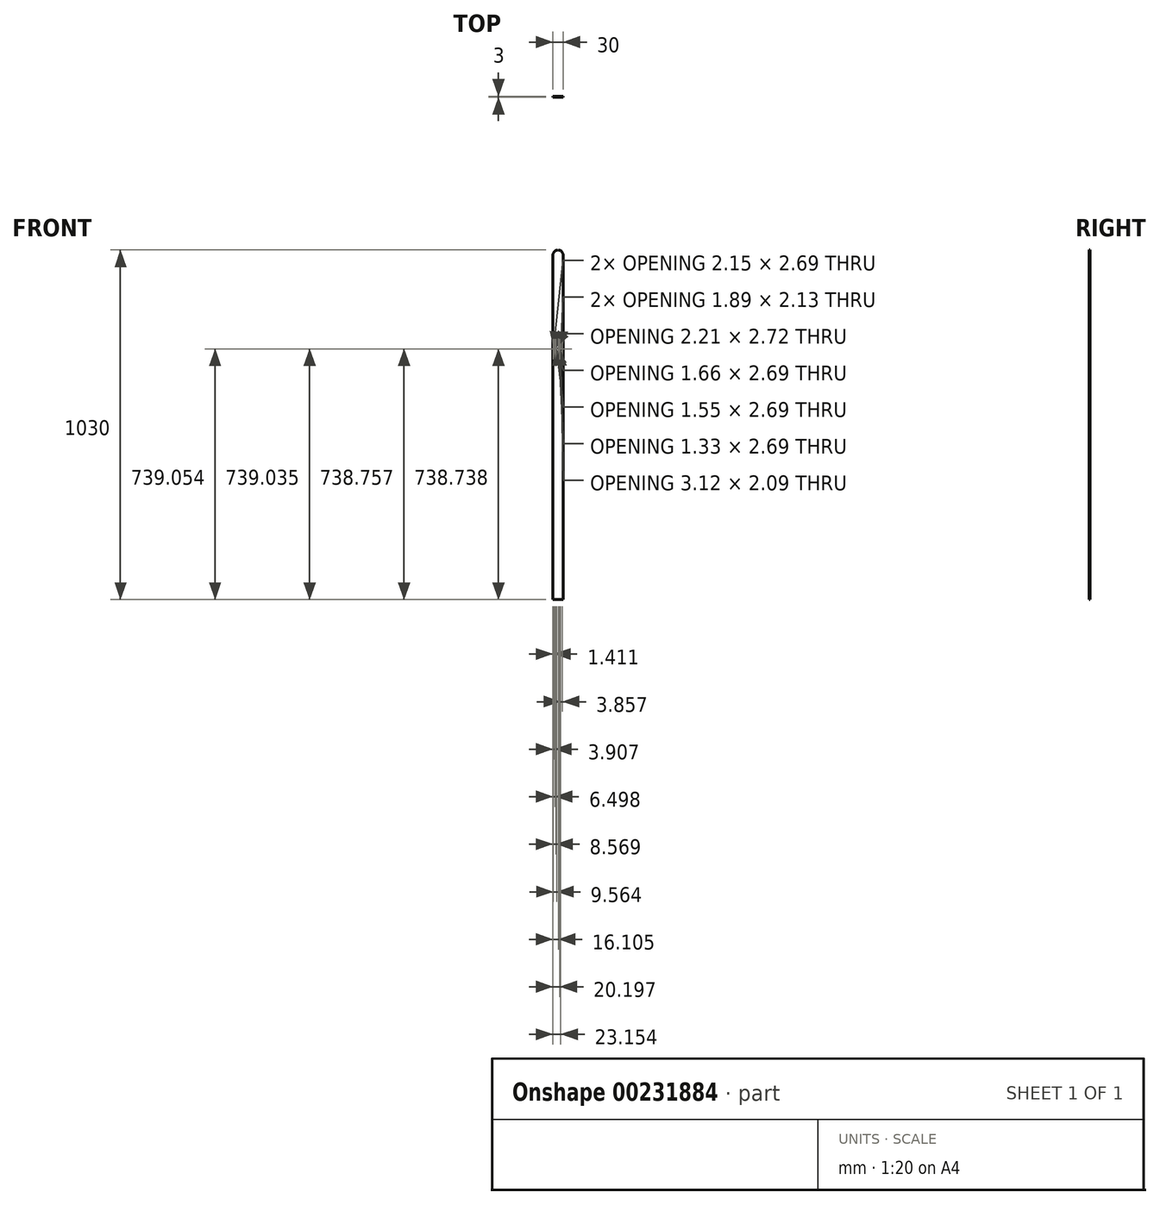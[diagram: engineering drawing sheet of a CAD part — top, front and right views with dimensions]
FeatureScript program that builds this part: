
annotation { "Feature Type Name" : "Feature", "Feature Type Description" : "" }
export const myFeature = defineFeature(function(context is Context, id is Id, definition is map)
    precondition{}
    {
        {
            var Q0;
            Q0=qCreatedBy(makeId("Front.planeOp"),FACE);
            var sketch = newSketch(context, id + "F0", { "sketchPlane" : qUnion([Q0])});
            skLineSegment(sketch, "E0.bottom", {"start": v(0, 0) * mm, "end": v(30, 0) * mm});
            skLineSegment(sketch, "E0.top", {"start": v(15, 1030) * mm, "end": v(15, 1030) * mm});
            skLineSegment(sketch, "E0.left", {"start": v(0, 0) * mm, "end": v(0, 1015) * mm});
            skLineSegment(sketch, "E0.right", {"start": v(30, 0) * mm, "end": v(30, 1015) * mm});
            skPoint(sketch, "E1.visualSharp", {"position": v(30, 1030) * mm});
            skArc(sketch, "E1.filletArc", {"start": v(30, 1015) * mm, "mid": v(25.6, 1025.6) * mm, "end": v(15, 1030) * mm});
            skPoint(sketch, "E2.visualSharp", {"position": v(0, 1030) * mm});
            skArc(sketch, "E2.filletArc", {"start": v(15, 1030) * mm, "mid": v(4.4, 1025.6) * mm, "end": v(0, 1015) * mm});
            skText(sketch, "E3", { "text": "RULER - 1 meter", "fontName": "OpenSans-Bold.ttf"});
            const initialGuessF0  = {"E3": [0, 0.73771, 1, 0, 0.00271]};
            skSetInitialGuess(sketch, initialGuessF0);
            skSolve(sketch);
        }
        {
            var Q0;
            Q0=makeQuery(id+"F0.imprint","IMPRINT",FACE,{"disambiguationData":[TD([[makeQuery(id+"F0.imprint","IMPRINT",EDGE,{"derivedFrom":sQuery(id+"F0.wireOp",EDGE,"E0.bottom")}),1.0]])]});
            extrude(context, id + "F1", {"entities" : qUnion([Q0]), "depth" : 3 * mm});
        }
    });
